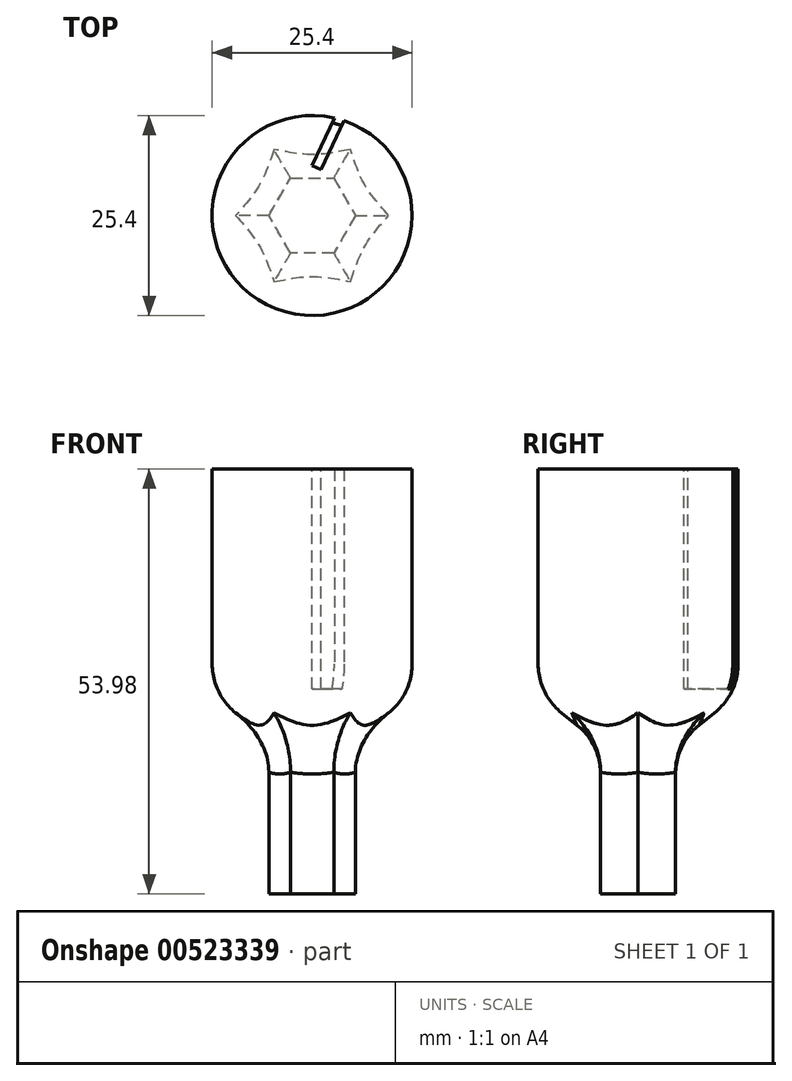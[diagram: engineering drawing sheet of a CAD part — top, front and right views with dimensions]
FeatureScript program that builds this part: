
annotation { "Feature Type Name" : "Feature", "Feature Type Description" : "" }
export const myFeature = defineFeature(function(context is Context, id is Id, definition is map)
    precondition{}
    {
        {
            var Q0;
            Q0=qCreatedBy(makeId("Top.planeOp"),FACE);
            var sketch = newSketch(context, id + "F0", { "sketchPlane" : qUnion([Q0])});
            skCircle(sketch, "E0.cCircle", {"center": v(0, 0) * mm, "radius": 4.76 * mm, "construction": true});
            skLineSegment(sketch, "E0.0", {"start": v(2.75, 4.76) * mm, "end": v(5.5, 0) * mm});
            skLineSegment(sketch, "E0.1", {"start": v(5.5, 0) * mm, "end": v(2.75, -4.76) * mm});
            skLineSegment(sketch, "E0.2", {"start": v(2.75, -4.76) * mm, "end": v(-2.75, -4.76) * mm});
            skLineSegment(sketch, "E0.3", {"start": v(-2.75, -4.76) * mm, "end": v(-5.5, 0) * mm});
            skLineSegment(sketch, "E0.4", {"start": v(-5.5, 0) * mm, "end": v(-2.75, 4.76) * mm});
            skLineSegment(sketch, "E0.5", {"start": v(-2.75, 4.76) * mm, "end": v(2.75, 4.76) * mm});
            skPoint(sketch, "E0.0.midPoint", {"position": v(4.12, 2.38) * mm});
            skSolve(sketch);
        }
        {
            var Q0;
            Q0 = qSketchRegion(id + "F0", true);
            extrude(context, id + "F1", {"entities" : qUnion([Q0]), "depth" : 25.4 * mm, "offsetDistance" : 25.4 * mm});
        }
        {
            var Q0;
            Q0=makeQuery(id+"F1.opExtrude","CAP_FACE",FACE,{"disambiguationData":[OSD([sQuery(id+"F0.wireOp",EDGE,"E0.0"),sQuery(id+"F0.wireOp",EDGE,"E0.1"),sQuery(id+"F0.wireOp",EDGE,"E0.2"),sQuery(id+"F0.wireOp",EDGE,"E0.3"),sQuery(id+"F0.wireOp",EDGE,"E0.4"),sQuery(id+"F0.wireOp",EDGE,"E0.5")])],"isStart":false});
            var sketch = newSketch(context, id + "F2", { "sketchPlane" : qUnion([Q0])});
            skCircle(sketch, "E1", {"center": v(0, 0) * mm, "radius": 12.7 * mm});
            skSolve(sketch);
        }
        {
            var Q0;
            Q0 = qSketchRegion(id + "F2", true);
            extrude(context, id + "F3", {"entities" : qUnion([Q0]), "operationType" : NewBodyOperationType.ADD, "depth" : 28.57 * mm, "offsetDistance" : 25.4 * mm});
        }
        {
            var Q0;
            Q0=qCreatedBy(makeId("Right.planeOp"),FACE);
            var sketch = newSketch(context, id + "F4", { "sketchPlane" : qUnion([Q0])});
            skLineSegment(sketch, "E2", {"start": v(4.76, 19.05) * mm, "end": v(12.7, 25.4) * mm});
            skLineSegment(sketch, "E3", {"start": v(12.7, 25.4) * mm, "end": v(4.76, 25.4) * mm});
            skLineSegment(sketch, "E4", {"start": v(4.76, 25.4) * mm, "end": v(4.76, 19.05) * mm});
            skLineSegment(sketch, "E5", {"start": v(0, 0) * mm, "end": v(0, 63.39) * mm, "construction": true});
            skSolve(sketch);
        }
        {
            var Q0;
            Q0=makeQuery(id+"F4.imprint","IMPRINT",FACE,{"disambiguationData":[TD([[makeQuery(id+"F4.imprint","IMPRINT",EDGE,{"derivedFrom":sQuery(id+"F4.wireOp",EDGE,"E2")}),1.0]])]});
            var Q1;
            Q1=sQuery(id+"F4.wireOp",EDGE,"E5");
            revolve(context, id + "F5", {"operationType" : NewBodyOperationType.ADD, "entities" : qUnion([Q0]), "axis" : qUnion([Q1]), "revolveType" : RevolveType.FULL});
        }
        {
            var Q0;
            Q0=makeQuery(id+"F5.boolean.opBoolean","MERGE",EDGE,{"derivedFrom":[makeQuery(id+"F3.opExtrude","CAP_EDGE",EDGE,{"disambiguationData":[OSD([sQuery(id+"F2.wireOp",EDGE,"E1")])],"isStart":true}),makeQuery(id+"F5.opRevolve","SWEPT_EDGE",EDGE,{"disambiguationData":[OSD([sQuery(id+"F4.wireOp",EDGE,"E2"),sQuery(id+"F4.wireOp",EDGE,"E3")])]})]});
            var Q1;
            Q1=makeQuery(id+"F5.opRevolve","SWEPT_FACE",FACE,{"disambiguationData":[OSD([sQuery(id+"F4.wireOp",EDGE,"E2")])]});
            fillet(context, id + "F6", {"entities" : qUnion([Q0, Q1]), "radius" : 7.94 * mm, "tangentPropagation" : true, "allowEdgeOverflow" : false});
        }
        {
            var Q0;
            Q0=makeQuery(id+"F3.opExtrude","CAP_FACE",FACE,{"disambiguationData":[OSD([sQuery(id+"F2.wireOp",EDGE,"E1")])],"isStart":false});
            var sketch = newSketch(context, id + "F7", { "sketchPlane" : qUnion([Q0])});
            skLineSegment(sketch, "E6", {"start": v(3.22, 13.26) * mm, "end": v(0, 6.35) * mm});
            skLineSegment(sketch, "E7", {"start": v(0, 6.35) * mm, "end": v(1.15, 5.81) * mm});
            skLineSegment(sketch, "E8", {"start": v(1.15, 5.81) * mm, "end": v(4.37, 12.72) * mm});
            skLineSegment(sketch, "E9", {"start": v(4.37, 12.72) * mm, "end": v(3.22, 13.26) * mm});
            skSolve(sketch);
        }
        {
            var Q0;
            Q0 = qSketchRegion(id + "F7", true);
            extrude(context, id + "F8", {"entities" : qUnion([Q0]), "operationType" : NewBodyOperationType.REMOVE, "oppositeDirection" : true, "depth" : 27.94 * mm, "offsetDistance" : 25.4 * mm});
        }
    });
